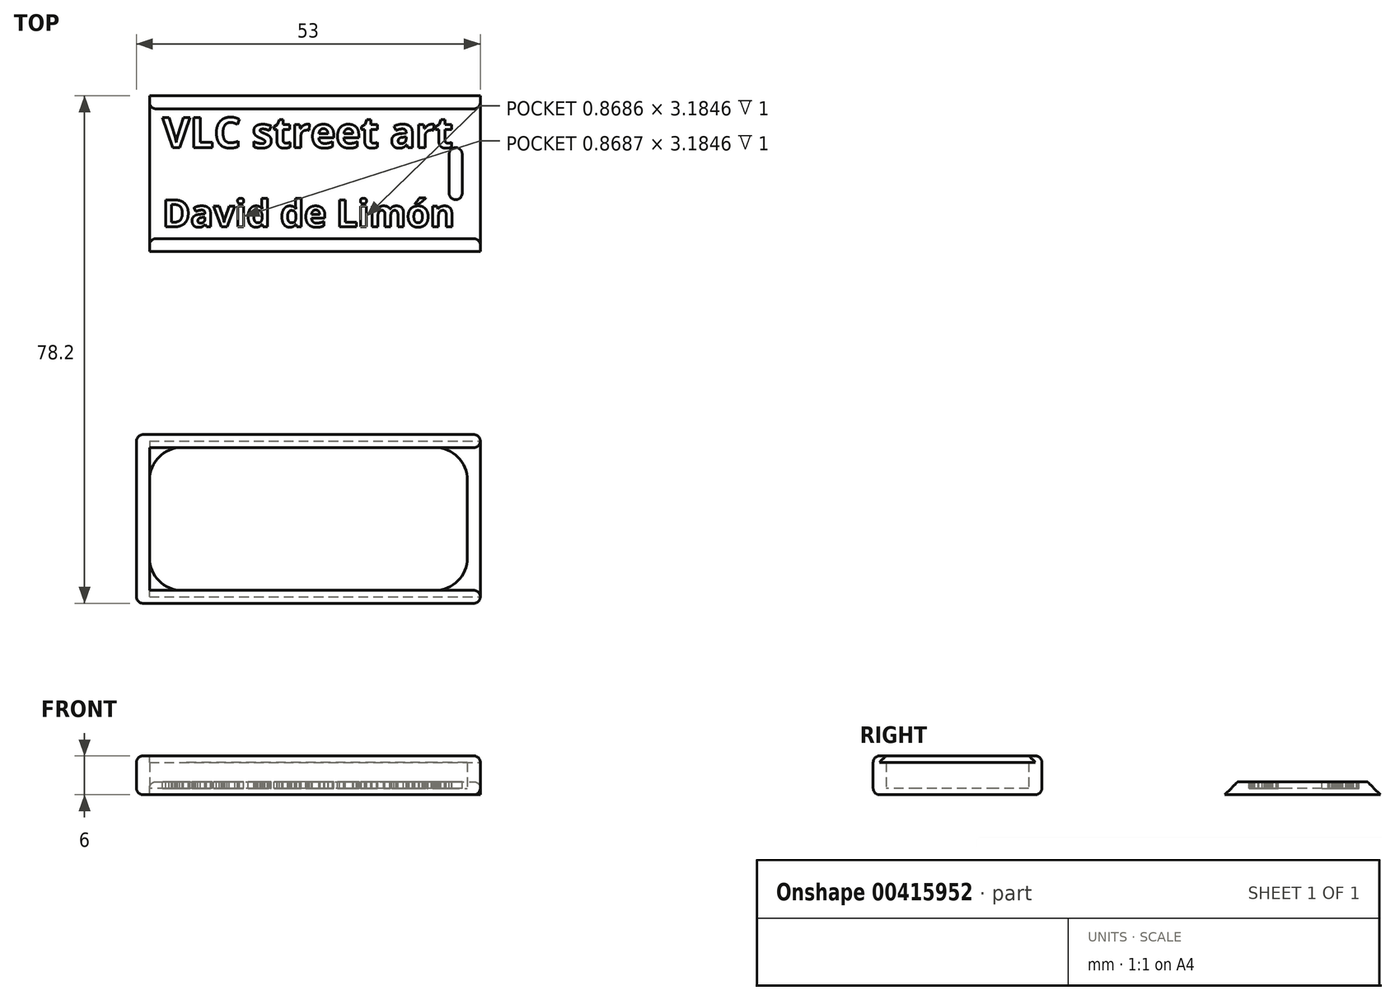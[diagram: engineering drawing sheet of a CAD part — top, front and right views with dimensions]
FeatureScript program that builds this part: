
annotation { "Feature Type Name" : "Feature", "Feature Type Description" : "" }
export const myFeature = defineFeature(function(context is Context, id is Id, definition is map)
    precondition{}
    {
        {
            assignVariable(context, id + "F0", {"name" : "Alto", "anyValue" : 2});
        }
        {
            assignVariable(context, id + "F1", {"name" : "largo", "anyValue" : 49});
        }
        {
            assignVariable(context, id + "F2", {"name" : "espesor", "anyValue" : 2});
        }
        {
            var Q0;
            Q0=qCreatedBy(makeId("Top.planeOp"),FACE);
            var sketch = newSketch(context, id + "F3", { "sketchPlane" : qUnion([Q0])});
            skLineSegment(sketch, "E0.bottom", {"start": v(24.5, 11) * mm, "end": v(-24.5, 11) * mm});
            skLineSegment(sketch, "E0.top", {"start": v(24.5, -11) * mm, "end": v(-24.5, -11) * mm});
            skLineSegment(sketch, "E0.left", {"start": v(24.5, 11) * mm, "end": v(24.5, -11) * mm});
            skLineSegment(sketch, "E0.right", {"start": v(-24.5, 11) * mm, "end": v(-24.5, -11) * mm});
            skPoint(sketch, "E0.middle", {"position": v(0, 0) * mm});
            skLineSegment(sketch, "E1.bottom", {"start": v(26.5, 13) * mm, "end": v(-26.5, 13) * mm});
            skLineSegment(sketch, "E1.top", {"start": v(26.5, -13) * mm, "end": v(-26.5, -13) * mm});
            skLineSegment(sketch, "E1.left", {"start": v(26.5, 13) * mm, "end": v(26.5, -13) * mm});
            skLineSegment(sketch, "E1.right", {"start": v(-26.5, 13) * mm, "end": v(-26.5, -13) * mm});
            skSolve(sketch);
        }
        {
            var Q0;
            Q0=makeQuery(id+"F3.imprint","IMPRINT",FACE,{"disambiguationData":[TD([[makeQuery(id+"F3.imprint","IMPRINT",EDGE,{"derivedFrom":sQuery(id+"F3.wireOp",EDGE,"E0.bottom")}),-1.0]])]});
            extrude(context, id + "F4", {"entities" : qUnion([Q0]), "depth" : (2 * getVariable(context, 'espesor') + getVariable(context, 'Alto')) * mm});
        }
        {
            var Q0;
            Q0=makeQuery(id+"F3.imprint","IMPRINT",FACE,{"disambiguationData":[TD([[makeQuery(id+"F3.imprint","IMPRINT",EDGE,{"derivedFrom":sQuery(id+"F3.wireOp",EDGE,"E0.bottom")}),1.0]])]});
            extrude(context, id + "F5", {"entities" : qUnion([Q0]), "operationType" : NewBodyOperationType.ADD, "depth" : (.5 * getVariable(context, 'espesor')) * mm});
        }
        {
            var Q0;
            Q0=makeQuery(id+"F4.opExtrude","SWEPT_FACE",FACE,{"disambiguationData":[OSD([sQuery(id+"F3.wireOp",EDGE,"E1.left")])]});
            var sketch = newSketch(context, id + "F6", { "sketchPlane" : qUnion([Q0])});
            skLineSegment(sketch, "E2", {"start": v(12, 5) * mm, "end": v(0, 5) * mm});
            skLineSegment(sketch, "E3", {"start": v(12, 5) * mm, "end": v(10, 7) * mm});
            skLineSegment(sketch, "E4", {"start": v(10, 7) * mm, "end": v(0, 7) * mm});
            skLineSegment(sketch, "E5.MirrorCS", {"start": v(-10, 7) * mm, "end": v(0, 7) * mm});
            skLineSegment(sketch, "E6.MirrorCS", {"start": v(-12, 5) * mm, "end": v(0, 5) * mm});
            skLineSegment(sketch, "E7.MirrorCS", {"start": v(-12, 5) * mm, "end": v(-10, 7) * mm});
            skSolve(sketch);
        }
        {
            var Q0;
            Q0=makeQuery(id+"F6.imprint","IMPRINT",FACE,{"disambiguationData":[TD([[makeQuery(id+"F6.imprint","IMPRINT",EDGE,{"derivedFrom":sQuery(id+"F6.wireOp",EDGE,"SvTivXyg-bIk5-CTMK-920A-VDUx7YFhp4Xd")}),1.0]])]});
            var Q1;
            {var subQ1=sQuery(id+"F6.wireOp",EDGE,"E4");Q1=makeQuery(id+"F6.imprint","IMPRINT",FACE,{"disambiguationData":[TD([[makeQuery(id+"F6.imprint","IMPRINT",EDGE,{"derivedFrom":subQ1}),1.0]])]});}
            var Q2;
            {var subQ5=sQuery(id+"F6.wireOp",EDGE,"E2");Q2=makeQuery(id+"F6.imprint","IMPRINT",FACE,{"disambiguationData":[TD([[makeQuery(id+"F6.imprint","IMPRINT",EDGE,{"derivedFrom":subQ5}),-1.0]])]});}
            extrude(context, id + "F7", {"entities" : qUnion([Q0, Q1, Q2]), "oppositeDirection" : true, "depth" : (getVariable(context, 'largo') + getVariable(context, 'espesor')) * mm});
        }
        {
            var Q0;
            Q0=makeQuery(id+"F7.opExtrude","SWEPT_BODY",BODY,{"disambiguationData":[OSD([sQuery(id+"F6.wireOp",EDGE,"SvTivXyg-bIk5-CTMK-920A-VDUx7YFhp4Xd"),sQuery(id+"F6.wireOp",EDGE,"NXYqkgHn-n5s3-E9hX-fx2y-YQDCVjQoqeno"),sQuery(id+"F6.wireOp",EDGE,"E2"),sQuery(id+"F6.wireOp",EDGE,"a3f9a05b-10ae-4f7d-80d1-88aed766babd0.MirrorCS"),sQuery(id+"F6.wireOp",EDGE,"1d98cbd7-637a-48a3-b701-6e80e332eecd0.MirrorCS"),sQuery(id+"F6.wireOp",EDGE,"f009dd86-6c0a-4020-9c2a-33f01825d16c0.MirrorCS")])]});
            transform(context, id + "F8", {"entities" : qUnion([Q0]), "transformType" : TransformType.TRANSLATION_3D, "dx" : 0 * mm, "dy" : 53.2 * mm, "dz" : 0 * mm, "makeCopy" : true});
        }
        {
            var Q0;
            Q0=makeQuery(id+"F4.opExtrude","SWEPT_EDGE",EDGE,{"disambiguationData":[OSD([sQuery(id+"F3.wireOp",EDGE,"E1.top"),sQuery(id+"F3.wireOp",EDGE,"E1.right")])]});
            var Q1;
            Q1=makeQuery(id+"F4.opExtrude","SWEPT_EDGE",EDGE,{"disambiguationData":[OSD([sQuery(id+"F3.wireOp",EDGE,"E1.bottom"),sQuery(id+"F3.wireOp",EDGE,"E1.right")])]});
            var Q2;
            Q2=makeQuery(id+"F4.opExtrude","SWEPT_EDGE",EDGE,{"disambiguationData":[OSD([sQuery(id+"F3.wireOp",EDGE,"E1.bottom"),sQuery(id+"F3.wireOp",EDGE,"E1.left")])]});
            var Q3;
            Q3=makeQuery(id+"F4.opExtrude","SWEPT_EDGE",EDGE,{"disambiguationData":[OSD([sQuery(id+"F3.wireOp",EDGE,"E1.top"),sQuery(id+"F3.wireOp",EDGE,"E1.left")])]});
            var Q4;
            Q4=makeQuery(id+"F4.opExtrude","CAP_EDGE",EDGE,{"disambiguationData":[OSD([sQuery(id+"F3.wireOp",EDGE,"E1.top")])],"isStart":false});
            var Q5;
            Q5=makeQuery(id+"F4.opExtrude","CAP_EDGE",EDGE,{"disambiguationData":[OSD([sQuery(id+"F3.wireOp",EDGE,"E1.bottom")])],"isStart":false});
            var Q6;
            Q6=makeQuery(id+"F4.opExtrude","CAP_EDGE",EDGE,{"disambiguationData":[OSD([sQuery(id+"F3.wireOp",EDGE,"E1.right")])],"isStart":false});
            var Q7;
            Q7=makeQuery(id+"F4.opExtrude","CAP_EDGE",EDGE,{"disambiguationData":[OSD([sQuery(id+"F3.wireOp",EDGE,"E1.top")])],"isStart":true});
            var Q8;
            Q8=makeQuery(id+"F4.opExtrude","CAP_EDGE",EDGE,{"disambiguationData":[OSD([sQuery(id+"F3.wireOp",EDGE,"E1.left")])],"isStart":true});
            var Q9;
            Q9=makeQuery(id+"F4.opExtrude","CAP_EDGE",EDGE,{"disambiguationData":[OSD([sQuery(id+"F3.wireOp",EDGE,"E1.bottom")])],"isStart":true});
            var Q10;
            Q10=makeQuery(id+"F4.opExtrude","CAP_EDGE",EDGE,{"disambiguationData":[OSD([sQuery(id+"F3.wireOp",EDGE,"E1.right")])],"isStart":true});
            var Q11;
            Q11=makeQuery(id+"F4.opExtrude","CAP_EDGE",EDGE,{"disambiguationData":[OSD([sQuery(id+"F3.wireOp",EDGE,"E1.left")])],"isStart":false});
            var Q12;
            Q12=makeQuery(id+"F8.opPattern","COPY",EDGE,{"derivedFrom":makeQuery(id+"F7.opExtrude","CAP_EDGE",EDGE,{"disambiguationData":[OSD([sQuery(id+"F6.wireOp",EDGE,"E4"),sQuery(id+"F6.wireOp",EDGE,"E5.MirrorCS")])],"isStart":false}),"instanceName":"1"});
            fillet(context, id + "F9", {"entities" : qUnion([Q0, Q1, Q2, Q3, Q4, Q5, Q6, Q7, Q8, Q9, Q10, Q11, Q12]), "radius" : 1 * mm, "tangentPropagation" : true, "allowEdgeOverflow" : false});
        }
        {
            var Q0;
            Q0=makeQuery(id+"F7.opExtrude","CAP_EDGE",EDGE,{"disambiguationData":[OSD([sQuery(id+"F6.wireOp",EDGE,"E4"),sQuery(id+"F6.wireOp",EDGE,"E5.MirrorCS")])],"isStart":true});
            var Q1;
            Q1=makeQuery(id+"F8.opPattern","COPY",EDGE,{"derivedFrom":makeQuery(id+"F7.opExtrude","CAP_EDGE",EDGE,{"disambiguationData":[OSD([sQuery(id+"F6.wireOp",EDGE,"E4"),sQuery(id+"F6.wireOp",EDGE,"E5.MirrorCS")])],"isStart":true}),"instanceName":"1"});
            fillet(context, id + "F10", {"entities" : qUnion([Q0, Q1]), "radius" : 1 * mm, "tangentPropagation" : true, "allowEdgeOverflow" : false});
        }
        {
            var Q0;
            Q0=makeQuery(id+"F7.opExtrude","SWEPT_BODY",BODY,{"disambiguationData":[OSD([sQuery(id+"F6.wireOp",EDGE,"SvTivXyg-bIk5-CTMK-920A-VDUx7YFhp4Xd"),sQuery(id+"F6.wireOp",EDGE,"NXYqkgHn-n5s3-E9hX-fx2y-YQDCVjQoqeno"),sQuery(id+"F6.wireOp",EDGE,"E2"),sQuery(id+"F6.wireOp",EDGE,"a3f9a05b-10ae-4f7d-80d1-88aed766babd0.MirrorCS"),sQuery(id+"F6.wireOp",EDGE,"1d98cbd7-637a-48a3-b701-6e80e332eecd0.MirrorCS"),sQuery(id+"F6.wireOp",EDGE,"f009dd86-6c0a-4020-9c2a-33f01825d16c0.MirrorCS")])]});
            var Q1;
            Q1=makeQuery(id+"F4.opExtrude","SWEPT_BODY",BODY,{"disambiguationData":[OSD([sQuery(id+"F3.wireOp",EDGE,"E0.bottom"),sQuery(id+"F3.wireOp",EDGE,"E0.top"),sQuery(id+"F3.wireOp",EDGE,"E0.left"),sQuery(id+"F3.wireOp",EDGE,"E0.right"),sQuery(id+"F3.wireOp",EDGE,"E1.bottom"),sQuery(id+"F3.wireOp",EDGE,"E1.top"),sQuery(id+"F3.wireOp",EDGE,"E1.left"),sQuery(id+"F3.wireOp",EDGE,"E1.right")])]});
            booleanBodies(context, id + "F11", {"operationType" : BooleanOperationType.SUBTRACTION, "tools" : qUnion([Q0]), "targets" : qUnion([Q1])});
        }
        {
            var Q0;
            Q0=makeQuery(id+"F8.opPattern","COPY",FACE,{"derivedFrom":makeQuery(id+"F7.opExtrude","SWEPT_FACE",FACE,{"disambiguationData":[OSD([sQuery(id+"F6.wireOp",EDGE,"E4"),sQuery(id+"F6.wireOp",EDGE,"E5.MirrorCS")])]}),"instanceName":"1"});
            var sketch = newSketch(context, id + "F12", { "sketchPlane" : qUnion([Q0])});
            skText(sketch, "E8", { "text": "VLC street art", "fontName": "OpenSans-Bold.ttf"});
            skText(sketch, "E9", { "text": "David de Limón", "fontName": "OpenSans-Bold.ttf"});
            skLineSegment(sketch, "E10", {"start": v(-24.5, 53.2) * mm, "end": v(25.5, 53.2) * mm, "construction": true});
            skLineSegment(sketch, "E11", {"start": v(0, 35.02) * mm, "end": v(0, 65.75) * mm, "construction": true});
            skPoint(sketch, "E11.endSnap0", {"position": v(0, 59.55) * mm});
            skLineSegment(sketch, "E12.bottom", {"start": v(23.7, 56.2) * mm, "end": v(21.7, 56.2) * mm});
            skLineSegment(sketch, "E12.top", {"start": v(23.7, 50.2) * mm, "end": v(21.7, 50.2) * mm});
            skLineSegment(sketch, "E12.left", {"start": v(23.7, 56.2) * mm, "end": v(23.7, 50.2) * mm});
            skLineSegment(sketch, "E12.right", {"start": v(21.7, 56.2) * mm, "end": v(21.7, 50.2) * mm});
            skPoint(sketch, "E12.middle", {"position": v(22.7, 53.2) * mm});
            skArc(sketch, "E13", {"start": v(23.7, 56.2) * mm, "mid": v(22.7, 57.22) * mm, "end": v(21.7, 56.2) * mm});
            skArc(sketch, "E14", {"start": v(21.7, 50.2) * mm, "mid": v(22.7, 49.2) * mm, "end": v(23.7, 50.2) * mm});
            const initialGuessF12  = {"E8": [-0.0225, 0.0572, 1, 0, 0.0047], "E9": [-0.0225, 0.045, 1, 0, 0.0042]};
            skSetInitialGuess(sketch, initialGuessF12);
            skSolve(sketch);
        }
        {
            var Q0;
            Q0 = qSketchRegion(id + "F12", true);
            extrude(context, id + "F13", {"entities" : qUnion([Q0]), "operationType" : NewBodyOperationType.REMOVE, "oppositeDirection" : true, "depth" : 1 * mm});
        }
        {
            var Q0;
            Q0=makeQuery(id+"F8.opPattern","COPY",BODY,{"derivedFrom":makeQuery(id+"F7.opExtrude","SWEPT_BODY",BODY,{"disambiguationData":[OSD([sQuery(id+"F6.wireOp",EDGE,"SvTivXyg-bIk5-CTMK-920A-VDUx7YFhp4Xd"),sQuery(id+"F6.wireOp",EDGE,"NXYqkgHn-n5s3-E9hX-fx2y-YQDCVjQoqeno"),sQuery(id+"F6.wireOp",EDGE,"E2"),sQuery(id+"F6.wireOp",EDGE,"a3f9a05b-10ae-4f7d-80d1-88aed766babd0.MirrorCS"),sQuery(id+"F6.wireOp",EDGE,"1d98cbd7-637a-48a3-b701-6e80e332eecd0.MirrorCS"),sQuery(id+"F6.wireOp",EDGE,"f009dd86-6c0a-4020-9c2a-33f01825d16c0.MirrorCS")])]}),"instanceName":"1"});
            transform(context, id + "F14", {"entities" : qUnion([Q0]), "transformType" : TransformType.TRANSLATION_3D, "dx" : 0 * mm, "dy" : 0 * mm, "dz" : -5 * mm, "makeCopy" : false});
        }
        {
            var Q0;
            Q0=makeQuery(id+"F4.opExtrude","SWEPT_EDGE",EDGE,{"disambiguationData":[OSD([sQuery(id+"F3.wireOp",EDGE,"E0.top"),sQuery(id+"F3.wireOp",EDGE,"E0.right")])]});
            var Q1;
            Q1=makeQuery(id+"F4.opExtrude","SWEPT_EDGE",EDGE,{"disambiguationData":[OSD([sQuery(id+"F3.wireOp",EDGE,"E0.bottom"),sQuery(id+"F3.wireOp",EDGE,"E0.left")])]});
            var Q2;
            Q2=makeQuery(id+"F4.opExtrude","SWEPT_EDGE",EDGE,{"disambiguationData":[OSD([sQuery(id+"F3.wireOp",EDGE,"E0.top"),sQuery(id+"F3.wireOp",EDGE,"E0.left")])]});
            var Q3;
            Q3=makeQuery(id+"F4.opExtrude","SWEPT_EDGE",EDGE,{"disambiguationData":[OSD([sQuery(id+"F3.wireOp",EDGE,"E0.bottom"),sQuery(id+"F3.wireOp",EDGE,"E0.right")])]});
            fillet(context, id + "F15", {"entities" : qUnion([Q0, Q1, Q2, Q3]), "radius" : 5 * mm, "tangentPropagation" : true, "allowEdgeOverflow" : false});
        }
    });
